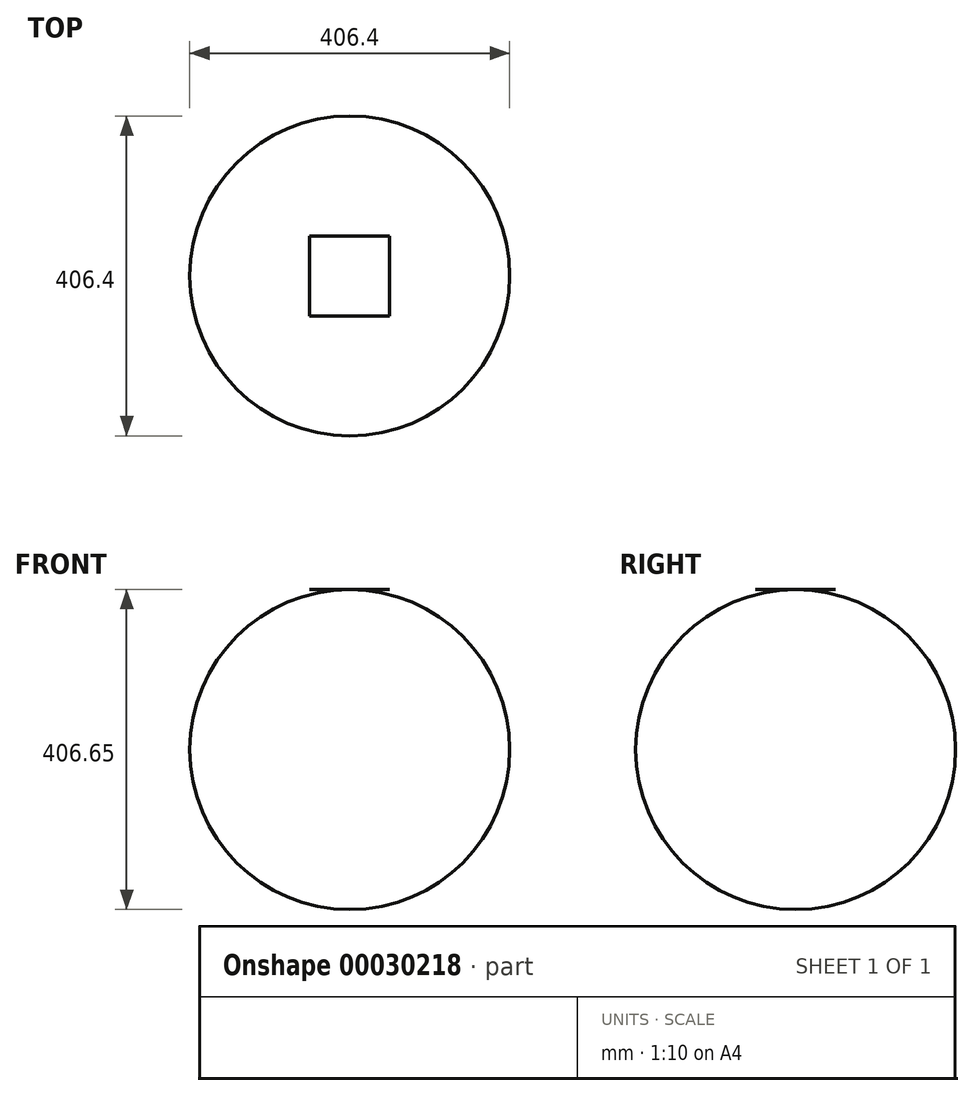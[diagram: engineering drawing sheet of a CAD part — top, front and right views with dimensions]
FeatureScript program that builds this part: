
annotation { "Feature Type Name" : "Feature", "Feature Type Description" : "" }
export const myFeature = defineFeature(function(context is Context, id is Id, definition is map)
    precondition{}
    {
        {
            var Q0;
            Q0=qCreatedBy(makeId("Top.planeOp"),FACE);
            var sketch = newSketch(context, id + "F0", { "sketchPlane" : qUnion([Q0])});
            skCircle(sketch, "E0", {"center": v(0, 0) * mm, "radius": 203.2 * mm});
            skLineSegment(sketch, "E1", {"start": v(-203.2, 0) * mm, "end": v(203.2, 0) * mm});
            skSolve(sketch);
        }
        {
            var Q0;
            {var subQ0=sQuery(id+"F0.wireOp",EDGE,"E1");Q0=makeQuery(id+"F0.imprint","IMPRINT",FACE,{"disambiguationData":[TD([[makeQuery(id+"F0.imprint","IMPRINT",EDGE,{"derivedFrom":subQ0}),-1.0]])]});}
            var Q1;
            Q1=sQuery(id+"F0.wireOp",EDGE,"E1");
            revolve(context, id + "F1", {"entities" : qUnion([Q0]), "axis" : qUnion([Q1]), "revolveType" : RevolveType.FULL});
        }
        {
            var Q0;
            Q0=qCreatedBy(makeId("Top.planeOp"),FACE);
            cPlane(context, id + "F2", {"entities" : qUnion([Q0]), "cplaneType" : CPlaneType.OFFSET, "offset" : 203.2 * mm, "width" : 152.4 * mm, "height" : 152.4 * mm});
        }
        {
            var Q0;
            Q0=qCreatedBy(id+"F2.planeOp",FACE);
            var sketch = newSketch(context, id + "F3", { "sketchPlane" : qUnion([Q0])});
            skLineSegment(sketch, "E2.rect.bottom", {"start": v(50.8, 50.8) * mm, "end": v(-50.8, 50.8) * mm});
            skLineSegment(sketch, "E2.rect.top", {"start": v(50.8, -50.8) * mm, "end": v(-50.8, -50.8) * mm});
            skLineSegment(sketch, "E2.rect.left", {"start": v(50.8, 50.8) * mm, "end": v(50.8, -50.8) * mm});
            skLineSegment(sketch, "E2.rect.right", {"start": v(-50.8, 50.8) * mm, "end": v(-50.8, -50.8) * mm});
            skPoint(sketch, "E2.rect.middle", {"position": v(0, 0) * mm});
            skSolve(sketch);
        }
        {
            var Q0;
            Q0 = qSketchRegion(id + "F3", true);
            extrude(context, id + "F4", {"entities" : qUnion([Q0]), "depth" : 0.25 * mm});
        }
    });
